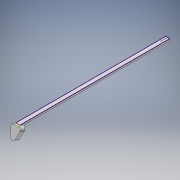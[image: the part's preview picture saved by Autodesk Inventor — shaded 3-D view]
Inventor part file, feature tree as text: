
AUTODESK INVENTOR PART (.ipt)
format: ipt  version: 2018.1 (Build 221171000, 171)  size: 215,040 bytes
history: native  units: mm
features: fillet x6, sketch x5, extrude x4, chamfer x2
ambient origin geometry x8: Origin, YZ Plane, XZ Plane, XY Plane, X Axis, Y Axis, Z Axis, Center Point
bodies: Solide1 (feature_tree)
feature tree (17):
  extrude  "Extrusion1"  Depth=839.2mm TaperAngle=0.0deg
  extrude  "Extrusion2"  Depth=30.0mm
  fillet  "Congé1"  Radius=70.0mm
  chamfer  "Chanfrein1"  Distance=3.490659mm
  chamfer  "Chanfrein2"  Distance=30.0mm
  fillet  "Congé2"  Radius=36.0mm
  fillet  "Congé3"  Radius=14.0mm
  fillet  "Congé4"  Radius=50.0mm
  fillet  "Congé5"  Radius=50.0mm
  fillet  "Congé6"  Radius=11.0mm
  extrude  "Extrusion3"  Depth=5.0mm
  extrude  "Extrusion4"  Depth=3.0mm
  sketch  "Esquisse9"
  sketch  "Esquisse1"
  sketch  "Esquisse2"
  sketch  "Esquisse5"
  sketch  "Esquisse6"
